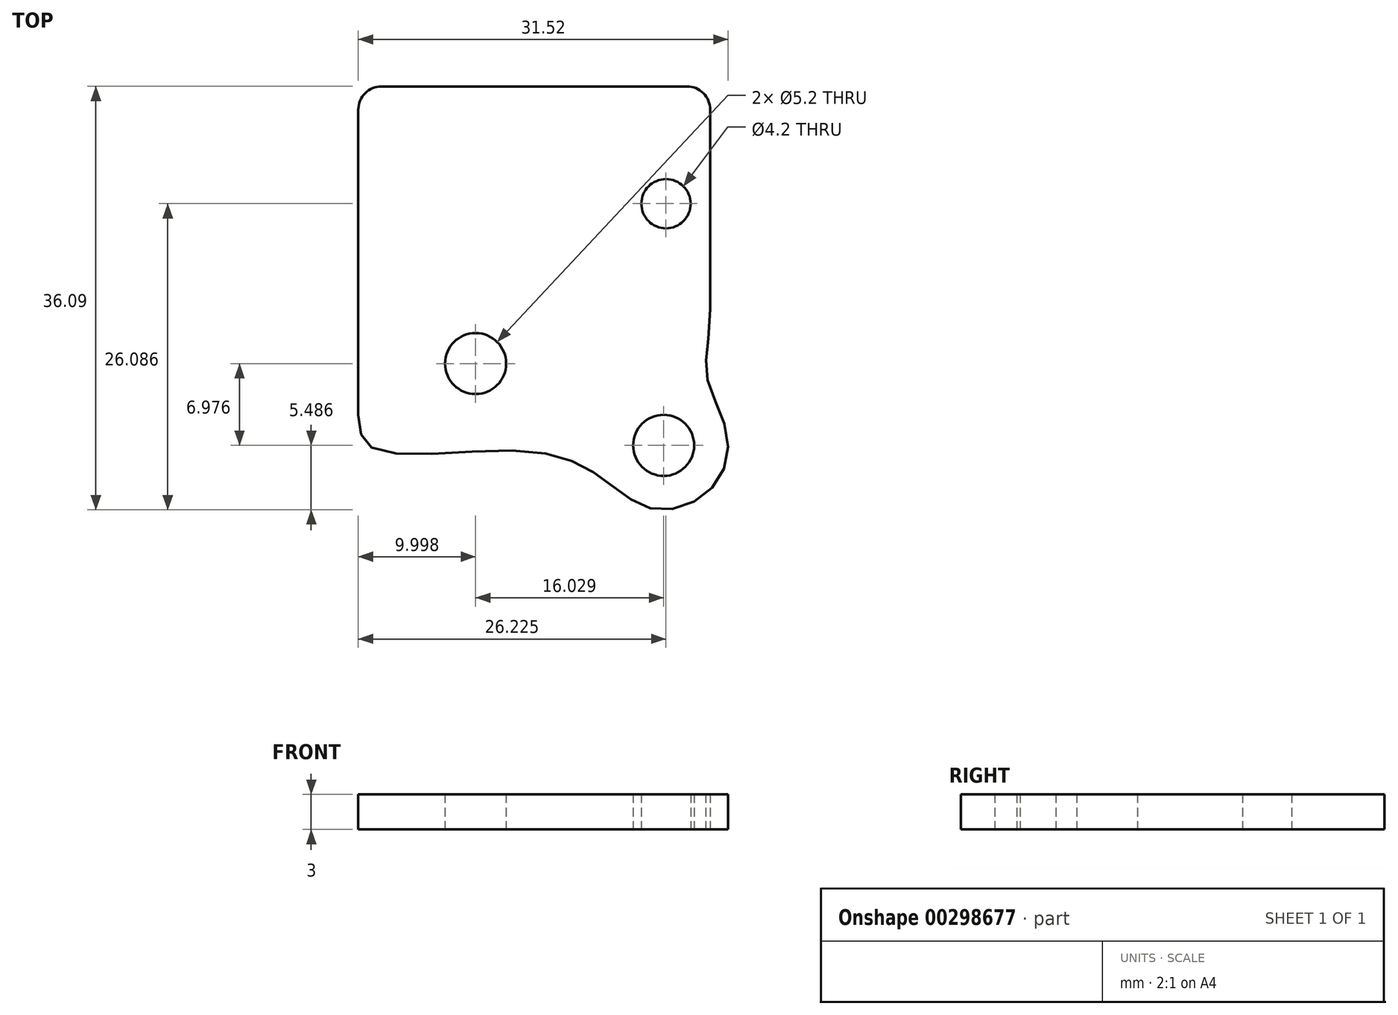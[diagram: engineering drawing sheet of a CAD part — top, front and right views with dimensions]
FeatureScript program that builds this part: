
annotation { "Feature Type Name" : "Feature", "Feature Type Description" : "" }
export const myFeature = defineFeature(function(context is Context, id is Id, definition is map)
    precondition{}
    {
        {
            var Q0;
            Q0=qCreatedBy(makeId("Top.planeOp"),FACE);
            var sketch = newSketch(context, id + "F0", { "sketchPlane" : qUnion([Q0])});
            skLineSegment(sketch, "E0.bottom", {"start": v(-13.65, 7.9) * mm, "end": v(12.35, 7.9) * mm});
            skLineSegment(sketch, "E0.left", {"start": v(-15.65, 5.9) * mm, "end": v(-15.65, -20.1) * mm});
            skLineSegment(sketch, "E0.right", {"start": v(14.35, 5.9) * mm, "end": v(14.35, -11.17) * mm});
            skCircle(sketch, "E1", {"center": v(10.57, -2.1) * mm, "radius": 2.1 * mm});
            skCircle(sketch, "E2", {"center": v(10.38, -22.7) * mm, "radius": 2.6 * mm});
            skPoint(sketch, "E3.orphan", {"position": v(14.35, -22.1) * mm});
            skPoint(sketch, "E4.visualSharp", {"position": v(-15.65, 7.9) * mm});
            skArc(sketch, "E4.filletArc", {"start": v(-13.65, 7.9) * mm, "mid": v(-15.07, 7.32) * mm, "end": v(-15.65, 5.9) * mm});
            skPoint(sketch, "E5.visualSharp", {"position": v(14.35, 7.9) * mm});
            skArc(sketch, "E5.filletArc", {"start": v(14.35, 5.9) * mm, "mid": v(13.76, 7.32) * mm, "end": v(12.35, 7.9) * mm});
            skPoint(sketch, "E6.visualSharp", {"position": v(14.35, -11.09) * mm});
            skPoint(sketch, "E7.visualSharp", {"position": v(-15.65, -22.1) * mm});
            skPoint(sketch, "E8.visualSharp", {"position": v(6.78, -30.02) * mm});
            skFitSpline(sketch, "E9", {"points": [v(-15.65, -20.1) * mm, v(-14.35, -22.97) * mm, v(-1.46, -23.18) * mm, v(5.2, -25.54) * mm, v(9.52, -28.1) * mm, v(14.22, -26.6) * mm, v(15.82, -22.08) * mm, v(14.06, -16.86) * mm, v(14.35, -11.09) * mm], "startDerivative": vector(2.52, -42.95) * mm, "endDerivative": vector(0.45, 68.55) * mm});
            skLineSegment(sketch, "E10", {"start": v(-5.65, -2.1) * mm, "end": v(36.16, -2.1) * mm, "construction": true});
            skLineSegment(sketch, "E11", {"start": v(36.16, -2.1) * mm, "end": v(36.16, -12.1) * mm, "construction": true});
            skLineSegment(sketch, "E12", {"start": v(36.16, -12.1) * mm, "end": v(-5.65, -12.1) * mm, "construction": true});
            skLineSegment(sketch, "E13", {"start": v(-5.65, -12.1) * mm, "end": v(-5.65, -2.1) * mm, "construction": true});
            skCircle(sketch, "E14", {"center": v(10.38, -22.7) * mm, "radius": 5.48 * mm, "construction": true});
            skCircle(sketch, "E15", {"center": v(-5.65, -15.72) * mm, "radius": 2.6 * mm});
            skSolve(sketch);
        }
        {
            var Q0;
            Q0=qSketchRegion(id+"F0",true);
            extrude(context, id + "F1", {"entities" : qUnion([Q0]), "depth" : 3 * mm});
        }
    });
